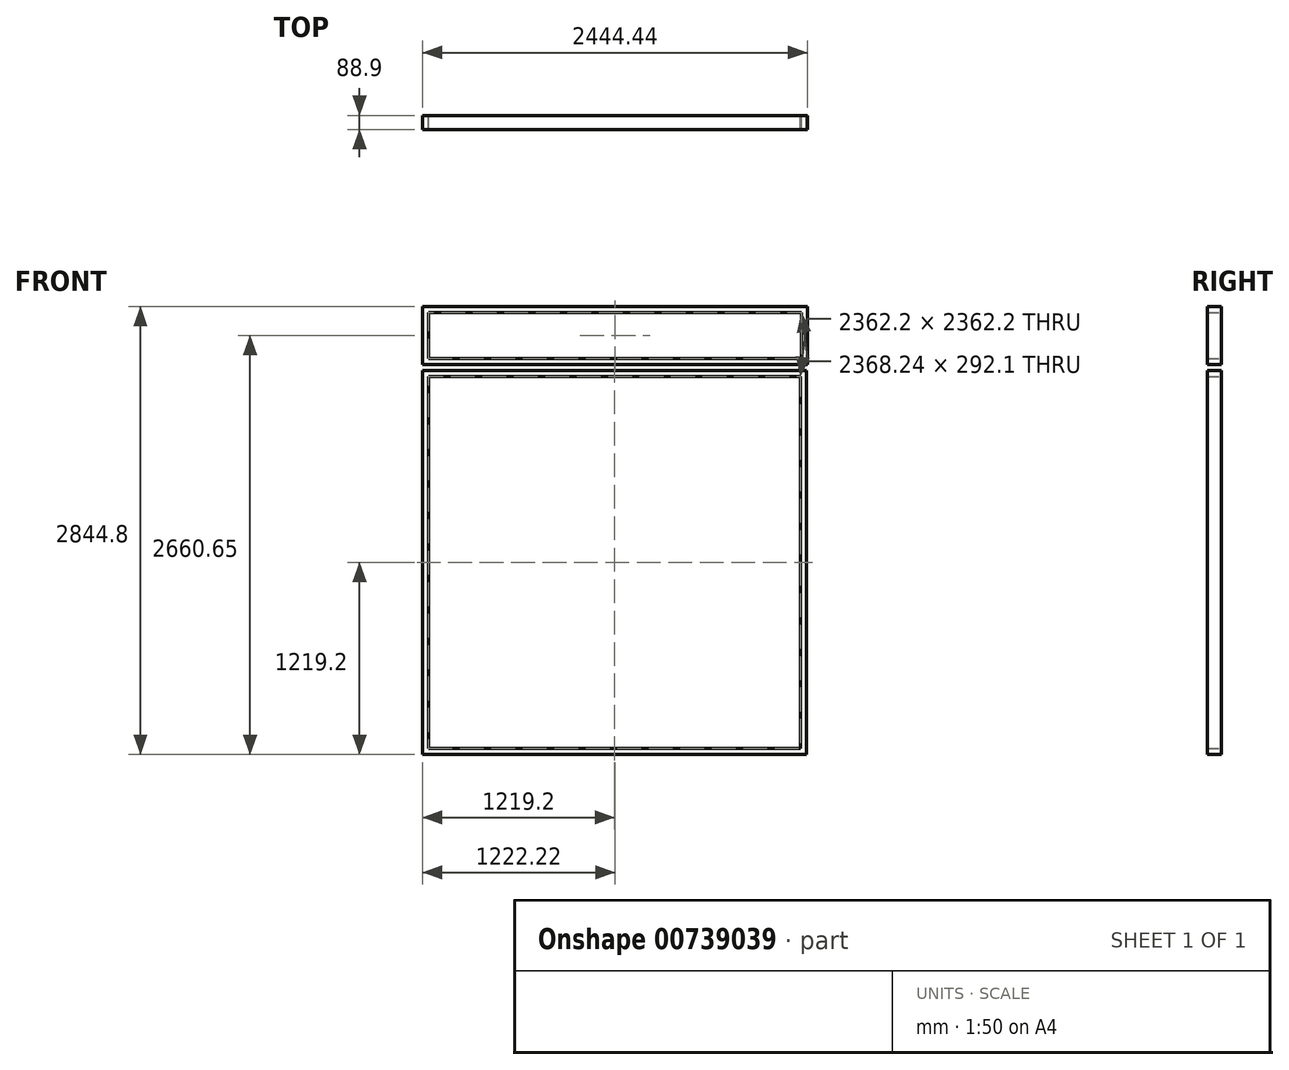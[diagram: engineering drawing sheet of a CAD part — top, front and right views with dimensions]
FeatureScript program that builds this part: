
annotation { "Feature Type Name" : "Feature", "Feature Type Description" : "" }
export const myFeature = defineFeature(function(context is Context, id is Id, definition is map)
    precondition{}
    {
        {
            var Q0;
            Q0=qCreatedBy(makeId("Front.planeOp"),FACE);
            var sketch = newSketch(context, id + "F0", { "sketchPlane" : qUnion([Q0])});
            skLineSegment(sketch, "E0.bottom", {"start": v(-1176.53, 1149.8) * mm, "end": v(1261.87, 1149.8) * mm});
            skLineSegment(sketch, "E0.top", {"start": v(-1176.53, -1288.6) * mm, "end": v(1261.87, -1288.6) * mm});
            skLineSegment(sketch, "E0.left", {"start": v(-1176.53, 1149.8) * mm, "end": v(-1176.53, -1288.6) * mm});
            skLineSegment(sketch, "E0.right", {"start": v(1261.87, 1149.8) * mm, "end": v(1261.87, -1288.6) * mm});
            skLineSegment(sketch, "E1.0", {"start": v(-1138.43, 1111.7) * mm, "end": v(1175.45, 1111.7) * mm});
            skLineSegment(sketch, "E2.0", {"start": v(-1138.43, 1111.7) * mm, "end": v(-1138.43, -1250.5) * mm});
            skLineSegment(sketch, "E2.1", {"start": v(-1138.43, 1111.7) * mm, "end": v(1223.77, 1111.7) * mm});
            skLineSegment(sketch, "E2.2", {"start": v(1223.77, 1111.7) * mm, "end": v(1223.77, -1250.5) * mm});
            skLineSegment(sketch, "E2.3", {"start": v(-1138.43, -1250.5) * mm, "end": v(1223.77, -1250.5) * mm});
            skLineSegment(sketch, "E3.bottom", {"start": v(-776.48, 1111.7) * mm, "end": v(-738.38, 1111.7) * mm});
            skLineSegment(sketch, "E3.top", {"start": v(-776.48, -1250.5) * mm, "end": v(-738.38, -1250.5) * mm});
            skLineSegment(sketch, "E3.left", {"start": v(-776.48, 1111.7) * mm, "end": v(-776.48, -1250.5) * mm});
            skLineSegment(sketch, "E3.right", {"start": v(-738.38, 1111.7) * mm, "end": v(-738.38, -1250.5) * mm});
            skLineSegment(sketch, "E4.bottom", {"start": v(-376.43, 1111.7) * mm, "end": v(-338.33, 1111.7) * mm});
            skLineSegment(sketch, "E4.top", {"start": v(-376.43, -1250.5) * mm, "end": v(-338.33, -1250.5) * mm});
            skLineSegment(sketch, "E4.left", {"start": v(-376.43, 1111.7) * mm, "end": v(-376.43, -1250.5) * mm});
            skLineSegment(sketch, "E4.right", {"start": v(-338.33, 1111.7) * mm, "end": v(-338.33, -1250.5) * mm});
            skLineSegment(sketch, "E5.bottom", {"start": v(23.62, 1111.7) * mm, "end": v(61.72, 1111.7) * mm});
            skLineSegment(sketch, "E5.top", {"start": v(23.62, -1250.5) * mm, "end": v(61.72, -1250.5) * mm});
            skLineSegment(sketch, "E5.left", {"start": v(23.62, 1111.7) * mm, "end": v(23.62, -1250.5) * mm});
            skLineSegment(sketch, "E5.right", {"start": v(61.72, 1111.7) * mm, "end": v(61.72, -1250.5) * mm});
            skLineSegment(sketch, "E6.bottom", {"start": v(461.77, 1111.7) * mm, "end": v(423.67, 1111.7) * mm});
            skLineSegment(sketch, "E6.top", {"start": v(461.77, -1250.5) * mm, "end": v(423.67, -1250.5) * mm});
            skLineSegment(sketch, "E6.left", {"start": v(461.77, 1111.7) * mm, "end": v(461.77, -1250.5) * mm});
            skLineSegment(sketch, "E6.right", {"start": v(423.67, 1111.7) * mm, "end": v(423.67, -1250.5) * mm});
            skLineSegment(sketch, "E7.bottom", {"start": v(823.72, 1111.7) * mm, "end": v(861.82, 1111.7) * mm});
            skLineSegment(sketch, "E7.top", {"start": v(823.72, -1250.5) * mm, "end": v(861.82, -1250.5) * mm});
            skLineSegment(sketch, "E7.left", {"start": v(823.72, 1111.7) * mm, "end": v(823.72, -1250.5) * mm});
            skLineSegment(sketch, "E7.right", {"start": v(861.82, 1111.7) * mm, "end": v(861.82, -1250.5) * mm});
            skLineSegment(sketch, "E8.top", {"start": v(-1176.53, 1187.9) * mm, "end": v(1261.87, 1187.9) * mm});
            skLineSegment(sketch, "E8.left", {"start": v(-1176.53, 1149.8) * mm, "end": v(-1176.53, 1187.9) * mm});
            skLineSegment(sketch, "E8.right", {"start": v(1261.87, 1149.8) * mm, "end": v(1261.87, 1187.9) * mm});
            skLineSegment(sketch, "E9.bottom", {"start": v(-1176.53, 1187.9) * mm, "end": v(1267.9, 1187.9) * mm});
            skLineSegment(sketch, "E9.top", {"start": v(-1176.53, 1556.2) * mm, "end": v(1267.9, 1556.2) * mm});
            skLineSegment(sketch, "E9.left", {"start": v(-1176.53, 1187.9) * mm, "end": v(-1176.53, 1556.2) * mm});
            skLineSegment(sketch, "E9.right", {"start": v(1267.9, 1187.9) * mm, "end": v(1267.9, 1556.2) * mm});
            skLineSegment(sketch, "E10.0", {"start": v(-1138.43, 1518.1) * mm, "end": v(1229.8, 1518.1) * mm});
            skLineSegment(sketch, "E10.1", {"start": v(-1138.43, 1226) * mm, "end": v(-1138.43, 1518.1) * mm});
            skLineSegment(sketch, "E10.2", {"start": v(-1138.43, 1226) * mm, "end": v(1229.8, 1226) * mm});
            skLineSegment(sketch, "E10.3", {"start": v(1229.8, 1226) * mm, "end": v(1229.8, 1518.1) * mm});
            skLineSegment(sketch, "E11.bottom", {"start": v(-784.75, 1518.1) * mm, "end": v(-746.65, 1518.1) * mm});
            skLineSegment(sketch, "E11.top", {"start": v(-784.75, 1226) * mm, "end": v(-746.65, 1226) * mm});
            skLineSegment(sketch, "E11.left", {"start": v(-784.75, 1518.1) * mm, "end": v(-784.75, 1226) * mm});
            skLineSegment(sketch, "E11.right", {"start": v(-746.65, 1518.1) * mm, "end": v(-746.65, 1226) * mm});
            skLineSegment(sketch, "E12.bottom", {"start": v(-365.06, 1518.1) * mm, "end": v(-326.96, 1518.1) * mm});
            skLineSegment(sketch, "E12.top", {"start": v(-365.06, 1226) * mm, "end": v(-326.96, 1226) * mm});
            skLineSegment(sketch, "E12.left", {"start": v(-365.06, 1518.1) * mm, "end": v(-365.06, 1226) * mm});
            skLineSegment(sketch, "E12.right", {"start": v(-326.96, 1518.1) * mm, "end": v(-326.96, 1226) * mm});
            skLineSegment(sketch, "E13.bottom", {"start": v(27.07, 1518.1) * mm, "end": v(65.17, 1518.1) * mm});
            skLineSegment(sketch, "E13.top", {"start": v(27.07, 1226) * mm, "end": v(65.17, 1226) * mm});
            skLineSegment(sketch, "E13.left", {"start": v(27.07, 1518.1) * mm, "end": v(27.07, 1226) * mm});
            skLineSegment(sketch, "E13.right", {"start": v(65.17, 1518.1) * mm, "end": v(65.17, 1226) * mm});
            skLineSegment(sketch, "E14.bottom", {"start": v(425.57, 1518.1) * mm, "end": v(463.67, 1518.1) * mm});
            skLineSegment(sketch, "E14.top", {"start": v(425.57, 1226) * mm, "end": v(463.67, 1226) * mm});
            skLineSegment(sketch, "E14.left", {"start": v(425.57, 1518.1) * mm, "end": v(425.57, 1226) * mm});
            skLineSegment(sketch, "E14.right", {"start": v(463.67, 1518.1) * mm, "end": v(463.67, 1226) * mm});
            skLineSegment(sketch, "E15.bottom", {"start": v(807.1, 1518.1) * mm, "end": v(845.2, 1518.1) * mm});
            skLineSegment(sketch, "E15.top", {"start": v(807.1, 1226) * mm, "end": v(845.2, 1226) * mm});
            skLineSegment(sketch, "E15.left", {"start": v(807.1, 1518.1) * mm, "end": v(807.1, 1226) * mm});
            skLineSegment(sketch, "E15.right", {"start": v(845.2, 1518.1) * mm, "end": v(845.2, 1226) * mm});
            skSolve(sketch);
        }
        {
            var Q0;
            Q0=makeQuery(id+"F0.imprint","IMPRINT",FACE,{"disambiguationData":[TD([[makeQuery(id+"F0.imprint","IMPRINT",EDGE,{"derivedFrom":sQuery(id+"F0.wireOp",EDGE,"E0.top")}),1.0]])]});
            var Q1;
            Q1=makeQuery(id+"F0.imprint","IMPRINT",FACE,{"disambiguationData":[TD([[makeQuery(id+"F0.imprint","IMPRINT",EDGE,{"derivedFrom":sQuery(id+"F0.wireOp",EDGE,"c1e748ae-7eef-4c04-b573-c81fa8028656.top")}),1.0]])]});
            var Q2;
            Q2=makeQuery(id+"F0.imprint","IMPRINT",FACE,{"disambiguationData":[TD([[makeQuery(id+"F0.imprint","IMPRINT",EDGE,{"derivedFrom":sQuery(id+"F0.wireOp",EDGE,"fa8f551a-b2f1-4d66-a69e-e12bf092d8e3.bottom")}),-1.0]])]});
            var Q3;
            Q3=makeQuery(id+"F0.imprint","IMPRINT",FACE,{"disambiguationData":[TD([[makeQuery(id+"F0.imprint","IMPRINT",EDGE,{"derivedFrom":sQuery(id+"F0.wireOp",EDGE,"E9.top")}),-1.0]])]});
            var Q4;
            Q4=makeQuery(id+"F0.imprint","IMPRINT",FACE,{"disambiguationData":[TD([[makeQuery(id+"F0.imprint","IMPRINT",EDGE,{"derivedFrom":sQuery(id+"F0.wireOp",EDGE,"E11.bottom")}),-1.0]])]});
            var Q5;
            Q5=makeQuery(id+"F0.imprint","IMPRINT",FACE,{"disambiguationData":[TD([[makeQuery(id+"F0.imprint","IMPRINT",EDGE,{"derivedFrom":sQuery(id+"F0.wireOp",EDGE,"3eec7f07-f543-479e-933e-edee64eff4d1.bottom")}),-1.0]])]});
            var Q6;
            Q6=makeQuery(id+"F0.imprint","IMPRINT",FACE,{"disambiguationData":[TD([[makeQuery(id+"F0.imprint","IMPRINT",EDGE,{"derivedFrom":sQuery(id+"F0.wireOp",EDGE,"E6.bottom")}),1.0]])]});
            var Q7;
            Q7=makeQuery(id+"F0.imprint","IMPRINT",FACE,{"disambiguationData":[TD([[makeQuery(id+"F0.imprint","IMPRINT",EDGE,{"derivedFrom":sQuery(id+"F0.wireOp",EDGE,"E7.bottom")}),-1.0]])]});
            var Q8;
            Q8=makeQuery(id+"F0.imprint","IMPRINT",FACE,{"disambiguationData":[TD([[makeQuery(id+"F0.imprint","IMPRINT",EDGE,{"derivedFrom":sQuery(id+"F0.wireOp",EDGE,"b82c4667-21d9-4e55-b3fd-54d73ae5b2c8.bottom")}),1.0]])]});
            var Q9;
            Q9=makeQuery(id+"F0.imprint","IMPRINT",FACE,{"disambiguationData":[TD([[makeQuery(id+"F0.imprint","IMPRINT",EDGE,{"derivedFrom":sQuery(id+"F0.wireOp",EDGE,"E0.bottom")}),1.0]])]});
            var Q10;
            Q10=makeQuery(id+"F0.imprint","IMPRINT",FACE,{"disambiguationData":[TD([[makeQuery(id+"F0.imprint","IMPRINT",EDGE,{"derivedFrom":sQuery(id+"F0.wireOp",EDGE,"a7f5fc44-c090-4f6f-80c6-fc873d8a056e.bottom")}),-1.0]])]});
            var Q11;
            Q11=makeQuery(id+"F0.imprint","IMPRINT",FACE,{"disambiguationData":[TD([[makeQuery(id+"F0.imprint","IMPRINT",EDGE,{"derivedFrom":sQuery(id+"F0.wireOp",EDGE,"435556ce-a4d7-410f-8cfc-4fd7b89beb88.bottom")}),1.0]])]});
            var Q12;
            Q12=makeQuery(id+"F0.imprint","IMPRINT",FACE,{"disambiguationData":[TD([[makeQuery(id+"F0.imprint","IMPRINT",EDGE,{"derivedFrom":sQuery(id+"F0.wireOp",EDGE,"E12.bottom")}),-1.0]])]});
            var Q13;
            Q13=makeQuery(id+"F0.imprint","IMPRINT",FACE,{"disambiguationData":[TD([[makeQuery(id+"F0.imprint","IMPRINT",EDGE,{"derivedFrom":sQuery(id+"F0.wireOp",EDGE,"58b1bf36-5a28-49fe-87df-e3cdce1c8a6e.bottom")}),-1.0]])]});
            var Q14;
            Q14=makeQuery(id+"F0.imprint","IMPRINT",FACE,{"disambiguationData":[TD([[makeQuery(id+"F0.imprint","IMPRINT",EDGE,{"derivedFrom":sQuery(id+"F0.wireOp",EDGE,"E4.bottom")}),-1.0]])]});
            var Q15;
            Q15=makeQuery(id+"F0.imprint","IMPRINT",FACE,{"disambiguationData":[TD([[makeQuery(id+"F0.imprint","IMPRINT",EDGE,{"derivedFrom":sQuery(id+"F0.wireOp",EDGE,"E5.bottom")}),-1.0]])]});
            var Q16;
            Q16=makeQuery(id+"F0.imprint","IMPRINT",FACE,{"disambiguationData":[TD([[makeQuery(id+"F0.imprint","IMPRINT",EDGE,{"derivedFrom":sQuery(id+"F0.wireOp",EDGE,"E13.bottom")}),-1.0]])]});
            var Q17;
            Q17=makeQuery(id+"F0.imprint","IMPRINT",FACE,{"disambiguationData":[TD([[makeQuery(id+"F0.imprint","IMPRINT",EDGE,{"derivedFrom":sQuery(id+"F0.wireOp",EDGE,"E3.bottom")}),-1.0]])]});
            var Q18;
            Q18=makeQuery(id+"F0.imprint","IMPRINT",FACE,{"disambiguationData":[TD([[makeQuery(id+"F0.imprint","IMPRINT",EDGE,{"derivedFrom":sQuery(id+"F0.wireOp",EDGE,"E14.bottom")}),-1.0]])]});
            var Q19;
            Q19=makeQuery(id+"F0.imprint","IMPRINT",FACE,{"disambiguationData":[TD([[makeQuery(id+"F0.imprint","IMPRINT",EDGE,{"derivedFrom":sQuery(id+"F0.wireOp",EDGE,"E15.bottom")}),-1.0]])]});
            extrude(context, id + "F1", {"entities" : qUnion([Q0, Q1, Q2, Q3, Q4, Q5, Q6, Q7, Q8, Q9, Q10, Q11, Q12, Q13, Q14, Q15, Q16, Q17, Q18, Q19]), "depth" : 88.9 * mm, "offsetDistance" : 25.4 * mm});
        }
    });
